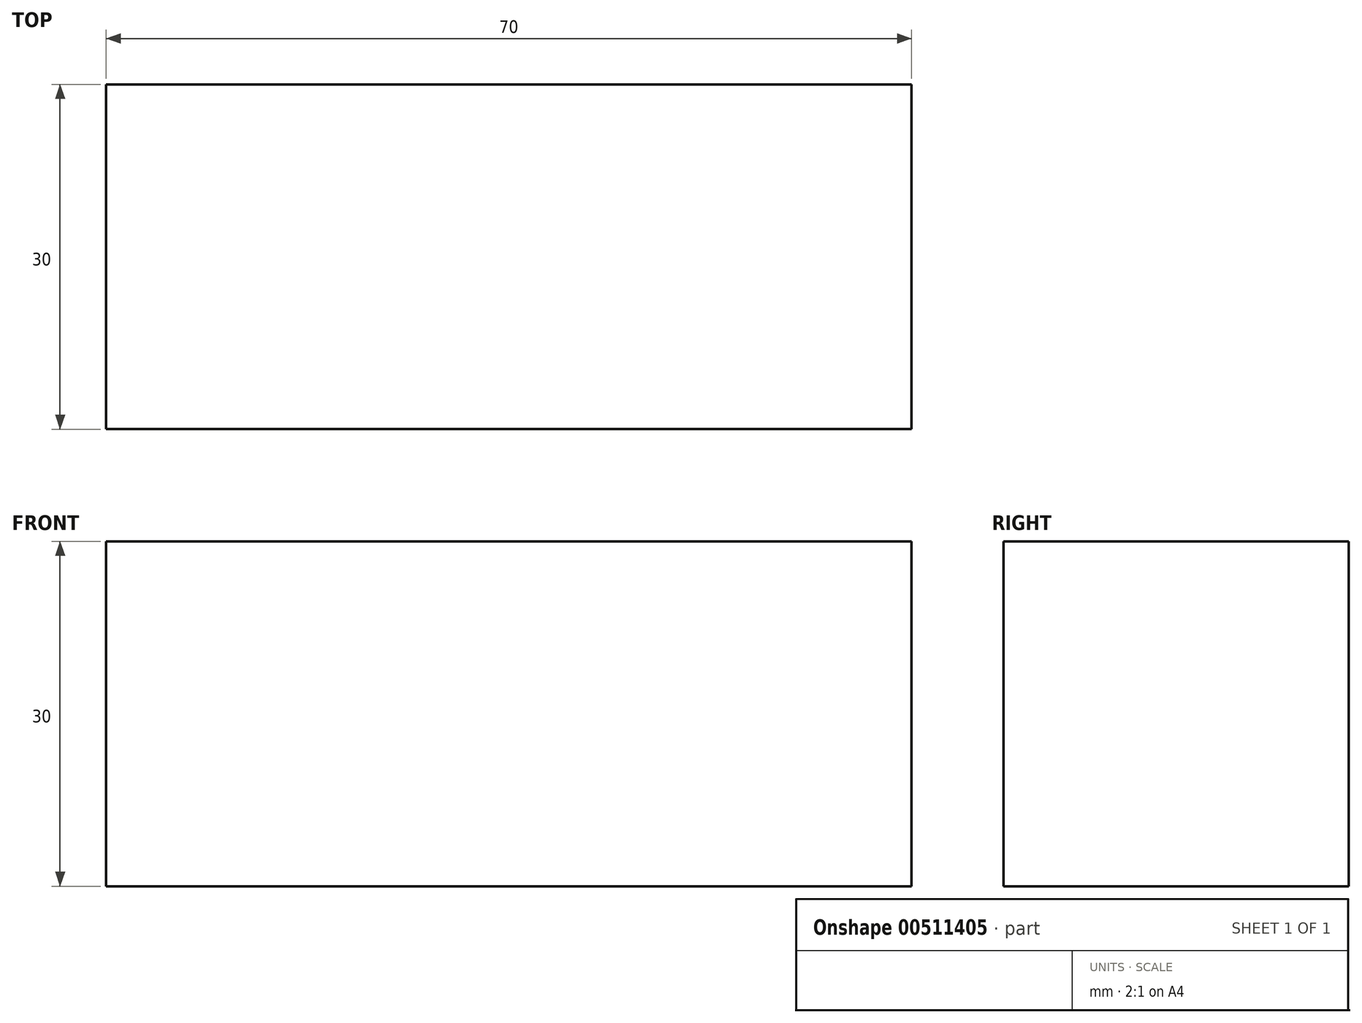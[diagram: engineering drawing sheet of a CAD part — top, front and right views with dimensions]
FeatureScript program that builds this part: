
annotation { "Feature Type Name" : "Feature", "Feature Type Description" : "" }
export const myFeature = defineFeature(function(context is Context, id is Id, definition is map)
    precondition{}
    {
        {
            var Q0;
            Q0=qCreatedBy(makeId("Top.planeOp"),FACE);
            var sketch = newSketch(context, id + "F0", { "sketchPlane" : qUnion([Q0])});
            skLineSegment(sketch, "E0.bottom", {"start": v(-29.5, 6.83) * mm, "end": v(40.5, 6.83) * mm});
            skLineSegment(sketch, "E0.top", {"start": v(-29.5, -23.17) * mm, "end": v(40.5, -23.17) * mm});
            skLineSegment(sketch, "E0.left", {"start": v(-29.5, 6.83) * mm, "end": v(-29.5, -23.17) * mm});
            skLineSegment(sketch, "E0.right", {"start": v(40.5, 6.83) * mm, "end": v(40.5, -23.17) * mm});
            skSolve(sketch);
        }
        {
            var Q0;
            Q0=makeQuery(id+"F0.imprint","IMPRINT",FACE,{"disambiguationData":[TD([[makeQuery(id+"F0.imprint","IMPRINT",EDGE,{"derivedFrom":sQuery(id+"F0.wireOp",EDGE,"E0.bottom")}),-1.0]])]});
            extrude(context, id + "F1", {"entities" : qUnion([Q0]), "depth" : 30 * mm});
        }
    });
